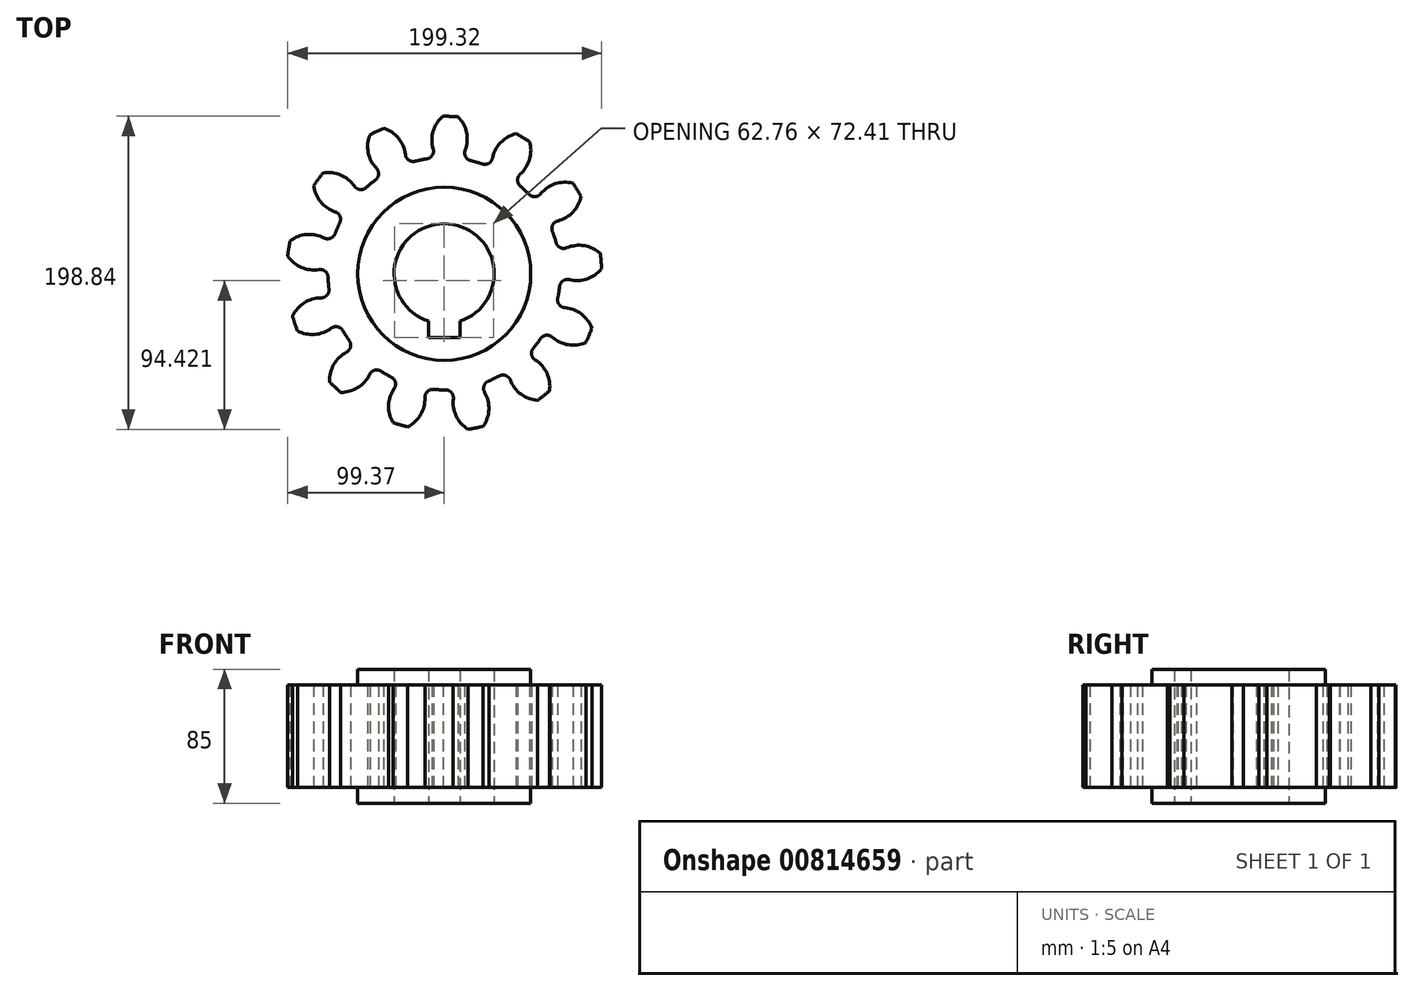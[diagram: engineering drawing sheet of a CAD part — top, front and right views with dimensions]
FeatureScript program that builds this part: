
annotation { "Feature Type Name" : "Feature", "Feature Type Description" : "" }
export const myFeature = defineFeature(function(context is Context, id is Id, definition is map)
    precondition{}
    {
        {
            var Q0;
            Q0=qCreatedBy(makeId("Top.planeOp"),FACE);
            var sketch = newSketch(context, id + "F0", { "sketchPlane" : qUnion([Q0])});
            skCircle(sketch, "E0", {"center": v(0, 0) * mm, "radius": 100 * mm});
            skSolve(sketch);
        }
        {
            var Q0;
            Q0=makeQuery(id+"F0.imprint","IMPRINT",FACE,{"disambiguationData":[TD([[makeQuery(id+"F0.imprint","IMPRINT",EDGE,{"derivedFrom":sQuery(id+"F0.wireOp",EDGE,"E0")}),1.0]])]});
            extrude(context, id + "F1", {"entities" : qUnion([Q0]), "oppositeDirection" : true, "depth" : 65 * mm, "offsetDistance" : 25 * mm});
        }
        {
            var Q0;
            Q0=makeQuery(id+"F1.opExtrude","CAP_FACE",FACE,{"disambiguationData":[OSD([sQuery(id+"F0.wireOp",EDGE,"E0")])],"isStart":true});
            var sketch = newSketch(context, id + "F2", { "sketchPlane" : qUnion([Q0])});
            skCircle(sketch, "E1", {"center": v(0, 0) * mm, "radius": 55 * mm});
            skSolve(sketch);
        }
        {
            var Q0;
            Q0=makeQuery(id+"F2.imprint","IMPRINT",FACE,{"disambiguationData":[TD([[makeQuery(id+"F2.imprint","IMPRINT",EDGE,{"derivedFrom":sQuery(id+"F2.wireOp",EDGE,"E1")}),1.0]])]});
            extrude(context, id + "F3", {"entities" : qUnion([Q0]), "operationType" : NewBodyOperationType.ADD, "depth" : 10 * mm, "offsetDistance" : 25 * mm});
        }
        {
            var Q0;
            Q0=makeQuery(id+"F1.opExtrude","CAP_FACE",FACE,{"disambiguationData":[OSD([sQuery(id+"F0.wireOp",EDGE,"E0")])],"isStart":false});
            var sketch = newSketch(context, id + "F4", { "sketchPlane" : qUnion([Q0])});
            skCircle(sketch, "E2", {"center": v(0, 0) * mm, "radius": 55 * mm});
            skSolve(sketch);
        }
        {
            var Q0;
            Q0=makeQuery(id+"F4.imprint","IMPRINT",FACE,{"disambiguationData":[TD([[makeQuery(id+"F4.imprint","IMPRINT",EDGE,{"derivedFrom":sQuery(id+"F4.wireOp",EDGE,"E2")}),1.0]])]});
            extrude(context, id + "F5", {"entities" : qUnion([Q0]), "operationType" : NewBodyOperationType.ADD, "depth" : 10 * mm, "offsetDistance" : 25 * mm});
        }
        {
            var Q0;
            Q0=makeQuery(id+"F5.opExtrude","CAP_FACE",FACE,{"disambiguationData":[OSD([sQuery(id+"F4.wireOp",EDGE,"E2")])],"isStart":false});
            var sketch = newSketch(context, id + "F6", { "sketchPlane" : qUnion([Q0])});
            skArc(sketch, "E3", {"start": v(-10, 30.17) * mm, "mid": v(0, -31.79) * mm, "end": v(10, 30.17) * mm});
            skLineSegment(sketch, "E4", {"start": v(-10, 30.17) * mm, "end": v(-10, 40.62) * mm});
            skLineSegment(sketch, "E5", {"start": v(-10, 40.62) * mm, "end": v(10, 40.62) * mm});
            skLineSegment(sketch, "E6", {"start": v(10, 40.62) * mm, "end": v(10, 30.17) * mm});
            skSolve(sketch);
        }
        {
            var Q0;
            Q0=makeQuery(id+"F6.imprint","IMPRINT",FACE,{"disambiguationData":[TD([[makeQuery(id+"F6.imprint","IMPRINT",EDGE,{"derivedFrom":sQuery(id+"F6.wireOp",EDGE,"E3")}),1.0]])]});
            extrude(context, id + "F7", {"entities" : qUnion([Q0]), "operationType" : NewBodyOperationType.REMOVE, "oppositeDirection" : true, "depth" : 100 * mm, "offsetDistance" : 25 * mm});
        }
        {
            var Q0;
            Q0=makeQuery(id+"F1.opExtrude","CAP_FACE",FACE,{"disambiguationData":[OSD([sQuery(id+"F0.wireOp",EDGE,"E0")])],"isStart":false});
            var sketch = newSketch(context, id + "F8", { "sketchPlane" : qUnion([Q0])});
            skArc(sketch, "E7", {"start": v(0.8, 73.79) * mm, "mid": v(-2.99, 73.73) * mm, "end": v(-6.76, 73.48) * mm});
            skArc(sketch, "E8", {"start": v(21.78, 101.46) * mm, "mid": v(-4.2, 103.69) * mm, "end": v(-29.92, 99.37) * mm});
            skArc(sketch, "E9", {"start": v(21.78, 101.46) * mm, "mid": v(9.47, 93.55) * mm, "end": v(5.8, 79.39) * mm});
            skArc(sketch, "E10.MirrorC", {"start": v(-29.92, 99.37) * mm, "mid": v(-17.01, 92.48) * mm, "end": v(-12.21, 78.66) * mm});
            skLineSegment(sketch, "E11.trimOffspring", {"start": v(-4.2, 103.69) * mm, "end": v(-4.32, 106.7) * mm, "construction": true});
            skPoint(sketch, "E12.visualSharp", {"position": v(-13.41, 72.56) * mm});
            skArc(sketch, "E12.filletArc", {"start": v(-12.21, 78.66) * mm, "mid": v(-10.66, 74.83) * mm, "end": v(-6.76, 73.48) * mm});
            skPoint(sketch, "E13.visualSharp", {"position": v(7.5, 73.4) * mm});
            skArc(sketch, "E13.filletArc", {"start": v(0.8, 73.79) * mm, "mid": v(4.57, 75.45) * mm, "end": v(5.8, 79.39) * mm});
            skArc(sketch, "E14.1.0", {"start": v(-27.87, 99.96) * mm, "mid": v(-51.9, 89.86) * mm, "end": v(-72.67, 74.08) * mm});
            skArc(sketch, "E14.1.1", {"start": v(-72.67, 74.08) * mm, "mid": v(-58.04, 73.98) * mm, "end": v(-47.37, 63.97) * mm});
            skArc(sketch, "E14.1.2", {"start": v(-27.87, 99.96) * mm, "mid": v(-35.09, 87.24) * mm, "end": v(-31.75, 73) * mm});
            skArc(sketch, "E14.1.3", {"start": v(-33.6, 65.7) * mm, "mid": v(-31.02, 68.93) * mm, "end": v(-31.75, 73) * mm});
            skArc(sketch, "E14.1.4", {"start": v(-47.37, 63.97) * mm, "mid": v(-44.21, 61.3) * mm, "end": v(-40.13, 61.92) * mm});
            skArc(sketch, "E14.1.5", {"start": v(-33.6, 65.7) * mm, "mid": v(-36.9, 63.9) * mm, "end": v(-40.13, 61.92) * mm});
            skArc(sketch, "E14.2.0", {"start": v(-71.13, 75.56) * mm, "mid": v(-87.72, 55.44) * mm, "end": v(-98.77, 31.83) * mm});
            skArc(sketch, "E14.2.1", {"start": v(-98.77, 31.83) * mm, "mid": v(-85.77, 38.53) * mm, "end": v(-71.67, 34.63) * mm});
            skArc(sketch, "E14.2.2", {"start": v(-71.13, 75.56) * mm, "mid": v(-71.6, 60.94) * mm, "end": v(-62.03, 49.88) * mm});
            skArc(sketch, "E14.2.3", {"start": v(-60.28, 42.57) * mm, "mid": v(-59.5, 46.62) * mm, "end": v(-62.03, 49.88) * mm});
            skArc(sketch, "E14.2.4", {"start": v(-71.67, 34.63) * mm, "mid": v(-67.64, 33.74) * mm, "end": v(-64.31, 36.18) * mm});
            skArc(sketch, "E14.2.5", {"start": v(-60.28, 42.57) * mm, "mid": v(-62.38, 39.43) * mm, "end": v(-64.31, 36.18) * mm});
            skArc(sketch, "E14.3.0", {"start": v(-98.1, 33.85) * mm, "mid": v(-103.44, 8.33) * mm, "end": v(-102.25, -17.72) * mm});
            skArc(sketch, "E14.3.1", {"start": v(-102.25, -17.72) * mm, "mid": v(-93.85, -5.74) * mm, "end": v(-79.55, -2.64) * mm});
            skArc(sketch, "E14.3.2", {"start": v(-98.1, 33.85) * mm, "mid": v(-91.73, 20.68) * mm, "end": v(-78.1, 15.34) * mm});
            skArc(sketch, "E14.3.3", {"start": v(-73.15, 9.68) * mm, "mid": v(-74.35, 13.63) * mm, "end": v(-78.1, 15.34) * mm});
            skArc(sketch, "E14.3.4", {"start": v(-79.55, -2.64) * mm, "mid": v(-75.57, -1.56) * mm, "end": v(-73.76, 2.15) * mm});
            skArc(sketch, "E14.3.5", {"start": v(-73.15, 9.68) * mm, "mid": v(-73.55, 5.92) * mm, "end": v(-73.76, 2.15) * mm});
            skArc(sketch, "E14.4.0", {"start": v(-102.6, -15.62) * mm, "mid": v(-95.46, -40.7) * mm, "end": v(-82.3, -63.2) * mm});
            skArc(sketch, "E14.4.1", {"start": v(-82.3, -63.2) * mm, "mid": v(-80.43, -48.7) * mm, "end": v(-69.21, -39.31) * mm});
            skArc(sketch, "E14.4.2", {"start": v(-102.6, -15.62) * mm, "mid": v(-90.83, -24.32) * mm, "end": v(-76.29, -22.72) * mm});
            skArc(sketch, "E14.4.3", {"start": v(-69.27, -25.43) * mm, "mid": v(-72.17, -22.48) * mm, "end": v(-76.29, -22.72) * mm});
            skArc(sketch, "E14.4.4", {"start": v(-69.21, -39.31) * mm, "mid": v(-66.2, -36.5) * mm, "end": v(-66.3, -32.38) * mm});
            skArc(sketch, "E14.4.5", {"start": v(-69.27, -25.43) * mm, "mid": v(-67.88, -28.94) * mm, "end": v(-66.3, -32.38) * mm});
            skArc(sketch, "E14.5.0", {"start": v(-83.58, -61.5) * mm, "mid": v(-65.61, -80.4) * mm, "end": v(-43.5, -94.22) * mm});
            skArc(sketch, "E14.5.1", {"start": v(-43.5, -94.22) * mm, "mid": v(-48.6, -80.5) * mm, "end": v(-43.02, -66.97) * mm});
            skArc(sketch, "E14.5.2", {"start": v(-83.58, -61.5) * mm, "mid": v(-69.12, -63.74) * mm, "end": v(-56.99, -55.57) * mm});
            skArc(sketch, "E14.5.3", {"start": v(-49.52, -54.7) * mm, "mid": v(-53.45, -53.45) * mm, "end": v(-56.99, -55.57) * mm});
            skArc(sketch, "E14.5.4", {"start": v(-43.02, -66.97) * mm, "mid": v(-41.65, -63.08) * mm, "end": v(-43.67, -59.48) * mm});
            skArc(sketch, "E14.5.5", {"start": v(-49.52, -54.7) * mm, "mid": v(-46.66, -57.17) * mm, "end": v(-43.67, -59.48) * mm});
            skArc(sketch, "E14.6.0", {"start": v(-45.43, -93.3) * mm, "mid": v(-20.73, -101.68) * mm, "end": v(5.27, -103.64) * mm});
            skArc(sketch, "E14.6.1", {"start": v(5.27, -103.64) * mm, "mid": v(-5.62, -93.86) * mm, "end": v(-6.97, -79.3) * mm});
            skArc(sketch, "E14.6.2", {"start": v(-45.43, -93.3) * mm, "mid": v(-31.59, -88.56) * mm, "end": v(-24.64, -75.69) * mm});
            skArc(sketch, "E14.6.3", {"start": v(-18.43, -71.45) * mm, "mid": v(-22.5, -72.16) * mm, "end": v(-24.64, -75.69) * mm});
            skArc(sketch, "E14.6.4", {"start": v(-6.97, -79.3) * mm, "mid": v(-7.56, -75.2) * mm, "end": v(-11.02, -72.96) * mm});
            skArc(sketch, "E14.6.5", {"start": v(-18.43, -71.45) * mm, "mid": v(-14.74, -72.3) * mm, "end": v(-11.02, -72.96) * mm});
            skArc(sketch, "E14.7.0", {"start": v(3.14, -103.73) * mm, "mid": v(28.9, -99.67) * mm, "end": v(52.83, -89.32) * mm});
            skArc(sketch, "E14.7.1", {"start": v(52.83, -89.32) * mm, "mid": v(38.65, -85.72) * mm, "end": v(30.68, -73.45) * mm});
            skArc(sketch, "E14.7.2", {"start": v(3.14, -103.73) * mm, "mid": v(13.2, -93.1) * mm, "end": v(13.36, -78.47) * mm});
            skArc(sketch, "E14.7.3", {"start": v(16.9, -71.83) * mm, "mid": v(13.62, -74.35) * mm, "end": v(13.36, -78.47) * mm});
            skArc(sketch, "E14.7.4", {"start": v(30.68, -73.45) * mm, "mid": v(28.26, -70.1) * mm, "end": v(24.15, -69.73) * mm});
            skArc(sketch, "E14.7.5", {"start": v(16.9, -71.83) * mm, "mid": v(20.55, -70.87) * mm, "end": v(24.15, -69.73) * mm});
            skArc(sketch, "E14.8.0", {"start": v(50.98, -90.39) * mm, "mid": v(71.9, -74.83) * mm, "end": v(88.28, -54.54) * mm});
            skArc(sketch, "E14.8.1", {"start": v(88.28, -54.54) * mm, "mid": v(74.06, -57.94) * mm, "end": v(61.3, -50.78) * mm});
            skArc(sketch, "E14.8.2", {"start": v(50.98, -90.39) * mm, "mid": v(54.94, -76.3) * mm, "end": v(48.3, -63.27) * mm});
            skArc(sketch, "E14.8.3", {"start": v(48.34, -55.76) * mm, "mid": v(46.61, -59.5) * mm, "end": v(48.3, -63.27) * mm});
            skArc(sketch, "E14.8.4", {"start": v(61.3, -50.78) * mm, "mid": v(57.6, -48.95) * mm, "end": v(53.79, -50.52) * mm});
            skArc(sketch, "E14.8.5", {"start": v(48.34, -55.76) * mm, "mid": v(51.13, -53.2) * mm, "end": v(53.79, -50.52) * mm});
            skArc(sketch, "E14.9.0", {"start": v(87.15, -56.34) * mm, "mid": v(98.44, -32.84) * mm, "end": v(103.52, -7.26) * mm});
            skArc(sketch, "E14.9.1", {"start": v(103.52, -7.26) * mm, "mid": v(92.5, -16.89) * mm, "end": v(77.87, -16.47) * mm});
            skArc(sketch, "E14.9.2", {"start": v(87.15, -56.34) * mm, "mid": v(84.11, -42.03) * mm, "end": v(72.17, -33.58) * mm});
            skArc(sketch, "E14.9.3", {"start": v(68.71, -26.9) * mm, "mid": v(68.93, -31.03) * mm, "end": v(72.17, -33.58) * mm});
            skArc(sketch, "E14.9.4", {"start": v(77.87, -16.47) * mm, "mid": v(73.75, -16.57) * mm, "end": v(71.1, -19.74) * mm});
            skArc(sketch, "E14.9.5", {"start": v(68.71, -26.9) * mm, "mid": v(70, -23.35) * mm, "end": v(71.1, -19.74) * mm});
            skArc(sketch, "E14.10.0", {"start": v(103.35, -9.39) * mm, "mid": v(102.43, 16.67) * mm, "end": v(95.04, 41.67) * mm});
            skArc(sketch, "E14.10.1", {"start": v(95.04, 41.67) * mm, "mid": v(89.75, 28.03) * mm, "end": v(76.6, 21.6) * mm});
            skArc(sketch, "E14.10.2", {"start": v(103.35, -9.39) * mm, "mid": v(94, 1.87) * mm, "end": v(79.5, 3.8) * mm});
            skArc(sketch, "E14.10.3", {"start": v(73.34, 8.1) * mm, "mid": v(75.45, 4.56) * mm, "end": v(79.5, 3.8) * mm});
            skArc(sketch, "E14.10.4", {"start": v(76.6, 21.6) * mm, "mid": v(73, 19.6) * mm, "end": v(72.13, 15.57) * mm});
            skArc(sketch, "E14.10.5", {"start": v(73.34, 8.1) * mm, "mid": v(72.83, 11.85) * mm, "end": v(72.13, 15.57) * mm});
            skArc(sketch, "E14.11.0", {"start": v(95.87, 39.71) * mm, "mid": v(82.95, 62.36) * mm, "end": v(64.78, 81.07) * mm});
            skArc(sketch, "E14.11.1", {"start": v(64.78, 81.07) * mm, "mid": v(66.44, 66.53) * mm, "end": v(57.8, 54.73) * mm});
            skArc(sketch, "E14.11.2", {"start": v(95.87, 39.71) * mm, "mid": v(82.37, 45.35) * mm, "end": v(68.63, 40.32) * mm});
            skArc(sketch, "E14.11.3", {"start": v(61.18, 41.27) * mm, "mid": v(64.69, 39.1) * mm, "end": v(68.63, 40.32) * mm});
            skArc(sketch, "E14.11.4", {"start": v(57.8, 54.73) * mm, "mid": v(55.53, 51.28) * mm, "end": v(56.63, 47.3) * mm});
            skArc(sketch, "E14.11.5", {"start": v(61.18, 41.27) * mm, "mid": v(58.98, 44.34) * mm, "end": v(56.63, 47.3) * mm});
            skArc(sketch, "E14.12.0", {"start": v(66.44, 79.72) * mm, "mid": v(44.47, 93.76) * mm, "end": v(19.69, 101.89) * mm});
            skArc(sketch, "E14.12.1", {"start": v(19.69, 101.89) * mm, "mid": v(27.91, 89.79) * mm, "end": v(25.74, 75.32) * mm});
            skArc(sketch, "E14.12.2", {"start": v(66.44, 79.72) * mm, "mid": v(51.86, 78.43) * mm, "end": v(42.04, 67.6) * mm});
            skArc(sketch, "E14.12.3", {"start": v(35, 64.97) * mm, "mid": v(39.1, 64.68) * mm, "end": v(42.04, 67.6) * mm});
            skArc(sketch, "E14.12.4", {"start": v(25.74, 75.32) * mm, "mid": v(25.34, 71.21) * mm, "end": v(28.16, 68.2) * mm});
            skArc(sketch, "E14.12.5", {"start": v(35, 64.97) * mm, "mid": v(31.62, 66.67) * mm, "end": v(28.16, 68.2) * mm});
            skSolve(sketch);
        }
        {
            var Q0;
            {var subQ6=sQuery(id+"F8.wireOp",EDGE,"E14.2.1");var subQ9=sQuery(id+"F8.wireOp",EDGE,"E14.3.0");var subQ10=makeQuery(id+"F8.imprint","INTERSECT",VERTEX,{"derivedFrom":[subQ6,subQ9]});Q0=makeQuery(id+"F8.imprint","IMPRINT",FACE,{"disambiguationData":[TD([[makeQuery(id+"F8.imprint","IMPRINT",EDGE,{"disambiguationData":[TD([[subQ10,-1.0]])],"derivedFrom":subQ6}),-1.0]])]});}
            var Q1;
            {var subQ0=sQuery(id+"F8.wireOp",EDGE,"E14.3.3");Q1=makeQuery(id+"F8.imprint","IMPRINT",FACE,{"disambiguationData":[TD([[makeQuery(id+"F8.imprint","IMPRINT",EDGE,{"derivedFrom":subQ0}),1.0]])]});}
            var Q2;
            {var subQ6=sQuery(id+"F8.wireOp",EDGE,"E14.1.1");var subQ9=sQuery(id+"F8.wireOp",EDGE,"E14.2.0");var subQ10=makeQuery(id+"F8.imprint","INTERSECT",VERTEX,{"derivedFrom":[subQ6,subQ9]});Q2=makeQuery(id+"F8.imprint","IMPRINT",FACE,{"disambiguationData":[TD([[makeQuery(id+"F8.imprint","IMPRINT",EDGE,{"disambiguationData":[TD([[subQ10,-1.0]])],"derivedFrom":subQ6}),-1.0]])]});}
            var Q3;
            {var subQ0=sQuery(id+"F8.wireOp",EDGE,"E14.2.3");Q3=makeQuery(id+"F8.imprint","IMPRINT",FACE,{"disambiguationData":[TD([[makeQuery(id+"F8.imprint","IMPRINT",EDGE,{"derivedFrom":subQ0}),1.0]])]});}
            var Q4;
            {var subQ6=sQuery(id+"F8.wireOp",EDGE,"E14.3.1");var subQ9=sQuery(id+"F8.wireOp",EDGE,"E14.4.0");var subQ10=makeQuery(id+"F8.imprint","INTERSECT",VERTEX,{"derivedFrom":[subQ6,subQ9]});Q4=makeQuery(id+"F8.imprint","IMPRINT",FACE,{"disambiguationData":[TD([[makeQuery(id+"F8.imprint","IMPRINT",EDGE,{"disambiguationData":[TD([[subQ10,-1.0]])],"derivedFrom":subQ6}),-1.0]])]});}
            var Q5;
            {var subQ0=sQuery(id+"F8.wireOp",EDGE,"E14.4.3");Q5=makeQuery(id+"F8.imprint","IMPRINT",FACE,{"disambiguationData":[TD([[makeQuery(id+"F8.imprint","IMPRINT",EDGE,{"derivedFrom":subQ0}),1.0]])]});}
            var Q6;
            {var subQ0=sQuery(id+"F8.wireOp",EDGE,"E14.1.3");Q6=makeQuery(id+"F8.imprint","IMPRINT",FACE,{"disambiguationData":[TD([[makeQuery(id+"F8.imprint","IMPRINT",EDGE,{"derivedFrom":subQ0}),1.0]])]});}
            var Q7;
            {var subQ6=sQuery(id+"F8.wireOp",EDGE,"E10.MirrorC");var subQ9=sQuery(id+"F8.wireOp",EDGE,"E14.1.0");var subQ10=makeQuery(id+"F8.imprint","INTERSECT",VERTEX,{"derivedFrom":[subQ6,subQ9]});Q7=makeQuery(id+"F8.imprint","IMPRINT",FACE,{"disambiguationData":[TD([[makeQuery(id+"F8.imprint","IMPRINT",EDGE,{"disambiguationData":[TD([[subQ10,-1.0]])],"derivedFrom":subQ6}),-1.0]])]});}
            var Q8;
            Q8=makeQuery(id+"F8.imprint","IMPRINT",FACE,{"disambiguationData":[TD([[makeQuery(id+"F8.imprint","IMPRINT",EDGE,{"derivedFrom":sQuery(id+"F8.wireOp",EDGE,"E7")}),-1.0]])]});
            var Q9;
            {var subQ1=sQuery(id+"F8.wireOp",EDGE,"E8");Q9=makeQuery(id+"F8.imprint","IMPRINT",FACE,{"disambiguationData":[TD([[makeQuery(id+"F8.imprint","IMPRINT",EDGE,{"derivedFrom":subQ1}),1.0]])]});}
            var Q10;
            {var subQ0=sQuery(id+"F8.wireOp",EDGE,"E14.10.3");Q10=makeQuery(id+"F8.imprint","IMPRINT",FACE,{"disambiguationData":[TD([[makeQuery(id+"F8.imprint","IMPRINT",EDGE,{"derivedFrom":subQ0}),1.0]])]});}
            var Q11;
            {var subQ6=sQuery(id+"F8.wireOp",EDGE,"E14.9.1");var subQ9=sQuery(id+"F8.wireOp",EDGE,"E14.10.0");var subQ10=makeQuery(id+"F8.imprint","INTERSECT",VERTEX,{"derivedFrom":[subQ6,subQ9]});Q11=makeQuery(id+"F8.imprint","IMPRINT",FACE,{"disambiguationData":[TD([[makeQuery(id+"F8.imprint","IMPRINT",EDGE,{"disambiguationData":[TD([[subQ10,-1.0]])],"derivedFrom":subQ6}),-1.0]])]});}
            var Q12;
            {var subQ7=sQuery(id+"F8.wireOp",EDGE,"E14.10.1");var subQ9=sQuery(id+"F8.wireOp",EDGE,"E14.11.0");var subQ11=makeQuery(id+"F8.imprint","INTERSECT",VERTEX,{"derivedFrom":[subQ7,subQ9]});Q12=makeQuery(id+"F8.imprint","IMPRINT",FACE,{"disambiguationData":[TD([[makeQuery(id+"F8.imprint","IMPRINT",EDGE,{"disambiguationData":[TD([[subQ11,-1.0]])],"derivedFrom":subQ7}),-1.0]])]});}
            var Q13;
            {var subQ0=sQuery(id+"F8.wireOp",EDGE,"E14.11.3");Q13=makeQuery(id+"F8.imprint","IMPRINT",FACE,{"disambiguationData":[TD([[makeQuery(id+"F8.imprint","IMPRINT",EDGE,{"derivedFrom":subQ0}),1.0]])]});}
            var Q14;
            {var subQ0=sQuery(id+"F8.wireOp",EDGE,"E14.7.3");Q14=makeQuery(id+"F8.imprint","IMPRINT",FACE,{"disambiguationData":[TD([[makeQuery(id+"F8.imprint","IMPRINT",EDGE,{"derivedFrom":subQ0}),1.0]])]});}
            var Q15;
            {var subQ6=sQuery(id+"F8.wireOp",EDGE,"E14.6.1");var subQ9=sQuery(id+"F8.wireOp",EDGE,"E14.7.0");var subQ10=makeQuery(id+"F8.imprint","INTERSECT",VERTEX,{"derivedFrom":[subQ6,subQ9]});Q15=makeQuery(id+"F8.imprint","IMPRINT",FACE,{"disambiguationData":[TD([[makeQuery(id+"F8.imprint","IMPRINT",EDGE,{"disambiguationData":[TD([[subQ10,-1.0]])],"derivedFrom":subQ6}),-1.0]])]});}
            var Q16;
            {var subQ0=sQuery(id+"F8.wireOp",EDGE,"E14.8.3");Q16=makeQuery(id+"F8.imprint","IMPRINT",FACE,{"disambiguationData":[TD([[makeQuery(id+"F8.imprint","IMPRINT",EDGE,{"derivedFrom":subQ0}),1.0]])]});}
            var Q17;
            {var subQ6=sQuery(id+"F8.wireOp",EDGE,"E14.7.1");var subQ9=sQuery(id+"F8.wireOp",EDGE,"E14.8.0");var subQ10=makeQuery(id+"F8.imprint","INTERSECT",VERTEX,{"derivedFrom":[subQ6,subQ9]});Q17=makeQuery(id+"F8.imprint","IMPRINT",FACE,{"disambiguationData":[TD([[makeQuery(id+"F8.imprint","IMPRINT",EDGE,{"disambiguationData":[TD([[subQ10,-1.0]])],"derivedFrom":subQ6}),-1.0]])]});}
            var Q18;
            {var subQ0=sQuery(id+"F8.wireOp",EDGE,"E14.9.3");Q18=makeQuery(id+"F8.imprint","IMPRINT",FACE,{"disambiguationData":[TD([[makeQuery(id+"F8.imprint","IMPRINT",EDGE,{"derivedFrom":subQ0}),1.0]])]});}
            var Q19;
            {var subQ6=sQuery(id+"F8.wireOp",EDGE,"E14.8.1");var subQ9=sQuery(id+"F8.wireOp",EDGE,"E14.9.0");var subQ10=makeQuery(id+"F8.imprint","INTERSECT",VERTEX,{"derivedFrom":[subQ6,subQ9]});Q19=makeQuery(id+"F8.imprint","IMPRINT",FACE,{"disambiguationData":[TD([[makeQuery(id+"F8.imprint","IMPRINT",EDGE,{"disambiguationData":[TD([[subQ10,-1.0]])],"derivedFrom":subQ6}),-1.0]])]});}
            var Q20;
            {var subQ0=sQuery(id+"F8.wireOp",EDGE,"E14.6.3");Q20=makeQuery(id+"F8.imprint","IMPRINT",FACE,{"disambiguationData":[TD([[makeQuery(id+"F8.imprint","IMPRINT",EDGE,{"derivedFrom":subQ0}),1.0]])]});}
            var Q21;
            {var subQ6=sQuery(id+"F8.wireOp",EDGE,"E14.5.1");var subQ9=sQuery(id+"F8.wireOp",EDGE,"E14.6.0");var subQ10=makeQuery(id+"F8.imprint","INTERSECT",VERTEX,{"derivedFrom":[subQ6,subQ9]});Q21=makeQuery(id+"F8.imprint","IMPRINT",FACE,{"disambiguationData":[TD([[makeQuery(id+"F8.imprint","IMPRINT",EDGE,{"disambiguationData":[TD([[subQ10,-1.0]])],"derivedFrom":subQ6}),-1.0]])]});}
            var Q22;
            {var subQ6=sQuery(id+"F8.wireOp",EDGE,"E14.4.1");var subQ9=sQuery(id+"F8.wireOp",EDGE,"E14.5.0");var subQ10=makeQuery(id+"F8.imprint","INTERSECT",VERTEX,{"derivedFrom":[subQ6,subQ9]});Q22=makeQuery(id+"F8.imprint","IMPRINT",FACE,{"disambiguationData":[TD([[makeQuery(id+"F8.imprint","IMPRINT",EDGE,{"disambiguationData":[TD([[subQ10,-1.0]])],"derivedFrom":subQ6}),-1.0]])]});}
            var Q23;
            {var subQ0=sQuery(id+"F8.wireOp",EDGE,"E14.5.3");Q23=makeQuery(id+"F8.imprint","IMPRINT",FACE,{"disambiguationData":[TD([[makeQuery(id+"F8.imprint","IMPRINT",EDGE,{"derivedFrom":subQ0}),1.0]])]});}
            var Q24;
            {var subQ1=sQuery(id+"F8.wireOp",EDGE,"E9");var subQ5=sQuery(id+"F8.wireOp",EDGE,"E14.12.0");var subQ6=makeQuery(id+"F8.imprint","INTERSECT",VERTEX,{"derivedFrom":[subQ1,subQ5]});Q24=makeQuery(id+"F8.imprint","IMPRINT",FACE,{"disambiguationData":[TD([[makeQuery(id+"F8.imprint","IMPRINT",EDGE,{"disambiguationData":[TD([[subQ6,-1.0]])],"derivedFrom":subQ1}),1.0]])]});}
            var Q25;
            {var subQ0=sQuery(id+"F8.wireOp",EDGE,"E14.12.3");Q25=makeQuery(id+"F8.imprint","IMPRINT",FACE,{"disambiguationData":[TD([[makeQuery(id+"F8.imprint","IMPRINT",EDGE,{"derivedFrom":subQ0}),1.0]])]});}
            extrude(context, id + "F9", {"entities" : qUnion([Q0, Q1, Q2, Q3, Q4, Q5, Q6, Q7, Q8, Q9, Q10, Q11, Q12, Q13, Q14, Q15, Q16, Q17, Q18, Q19, Q20, Q21, Q22, Q23, Q24, Q25]), "operationType" : NewBodyOperationType.REMOVE, "oppositeDirection" : true, "depth" : 100 * mm, "offsetDistance" : 25 * mm});
        }
    });
